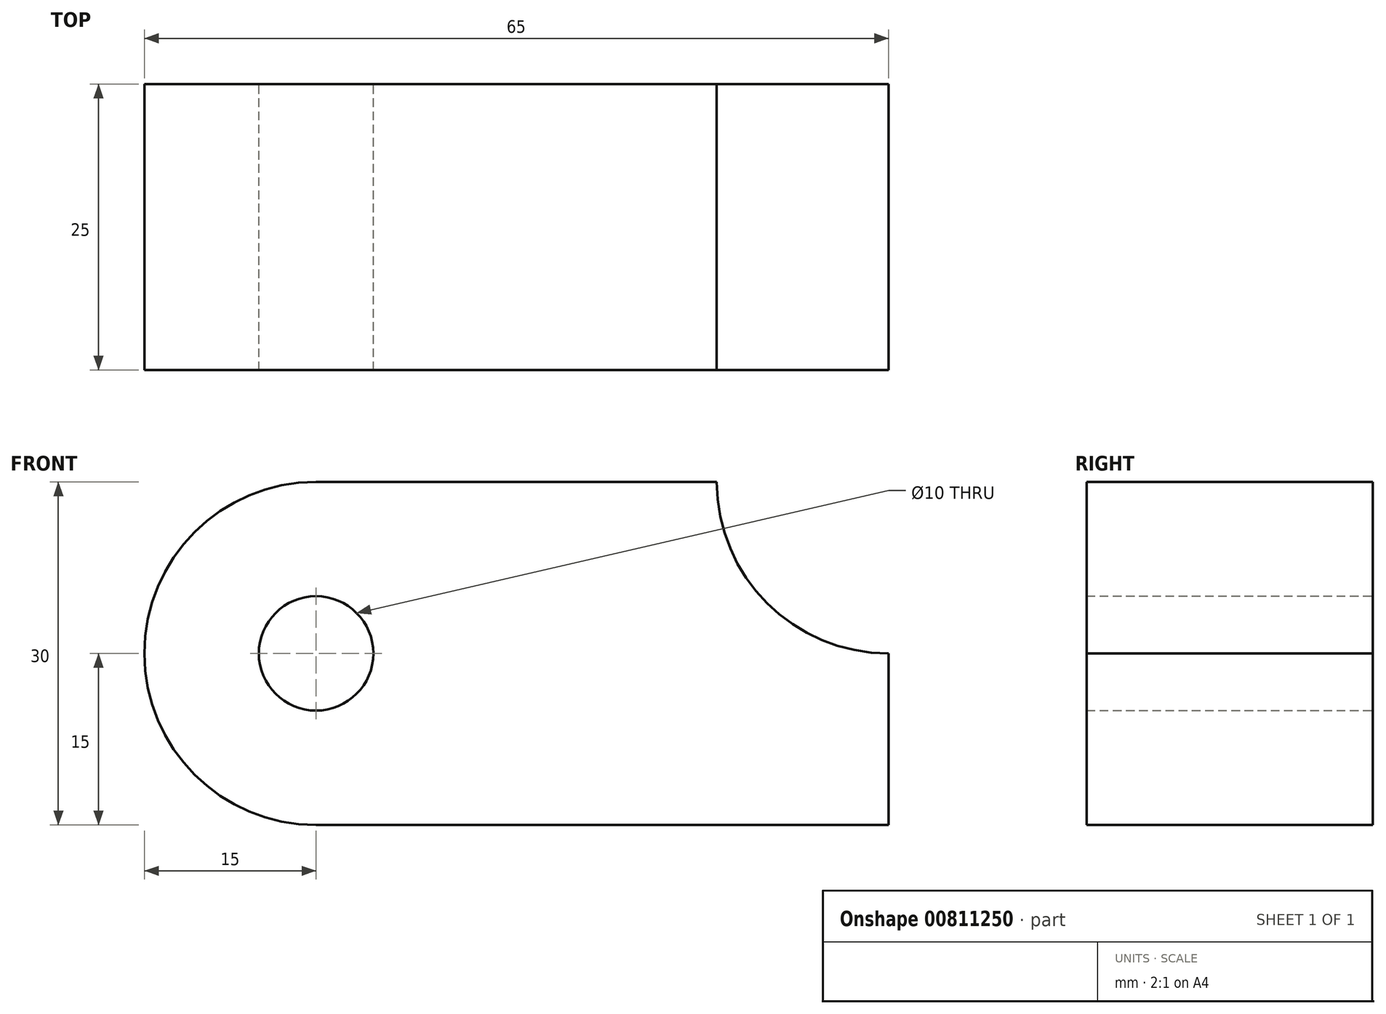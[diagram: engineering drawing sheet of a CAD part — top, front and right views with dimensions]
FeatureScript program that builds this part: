
annotation { "Feature Type Name" : "Feature", "Feature Type Description" : "" }
export const myFeature = defineFeature(function(context is Context, id is Id, definition is map)
    precondition{}
    {
        {
            var Q0;
            Q0=qCreatedBy(makeId("Front.planeOp"),FACE);
            var sketch = newSketch(context, id + "F0", { "sketchPlane" : qUnion([Q0])});
            skCircle(sketch, "E0", {"center": v(0, 0) * mm, "radius": 5 * mm});
            skArc(sketch, "E1", {"start": v(0, 15) * mm, "mid": v(-15, 0) * mm, "end": v(0, -15) * mm});
            skLineSegment(sketch, "E2", {"start": v(0, 15) * mm, "end": v(35, 15) * mm});
            skLineSegment(sketch, "E3", {"start": v(50, 0) * mm, "end": v(50, -15) * mm});
            skLineSegment(sketch, "E4", {"start": v(0, -15) * mm, "end": v(50, -15) * mm});
            skArc(sketch, "E5", {"start": v(35, 15) * mm, "mid": v(39.4, 4.4) * mm, "end": v(50, 0) * mm});
            skSolve(sketch);
        }
        {
            var Q0;
            Q0=makeQuery(id+"F0.imprint","IMPRINT",FACE,{"disambiguationData":[TD([[makeQuery(id+"F0.imprint","IMPRINT",EDGE,{"derivedFrom":sQuery(id+"F0.wireOp",EDGE,"E0")}),-1.0]])]});
            extrude(context, id + "F1", {"entities" : qUnion([Q0]), "depth" : 25 * mm, "offsetDistance" : 25 * mm});
        }
    });
